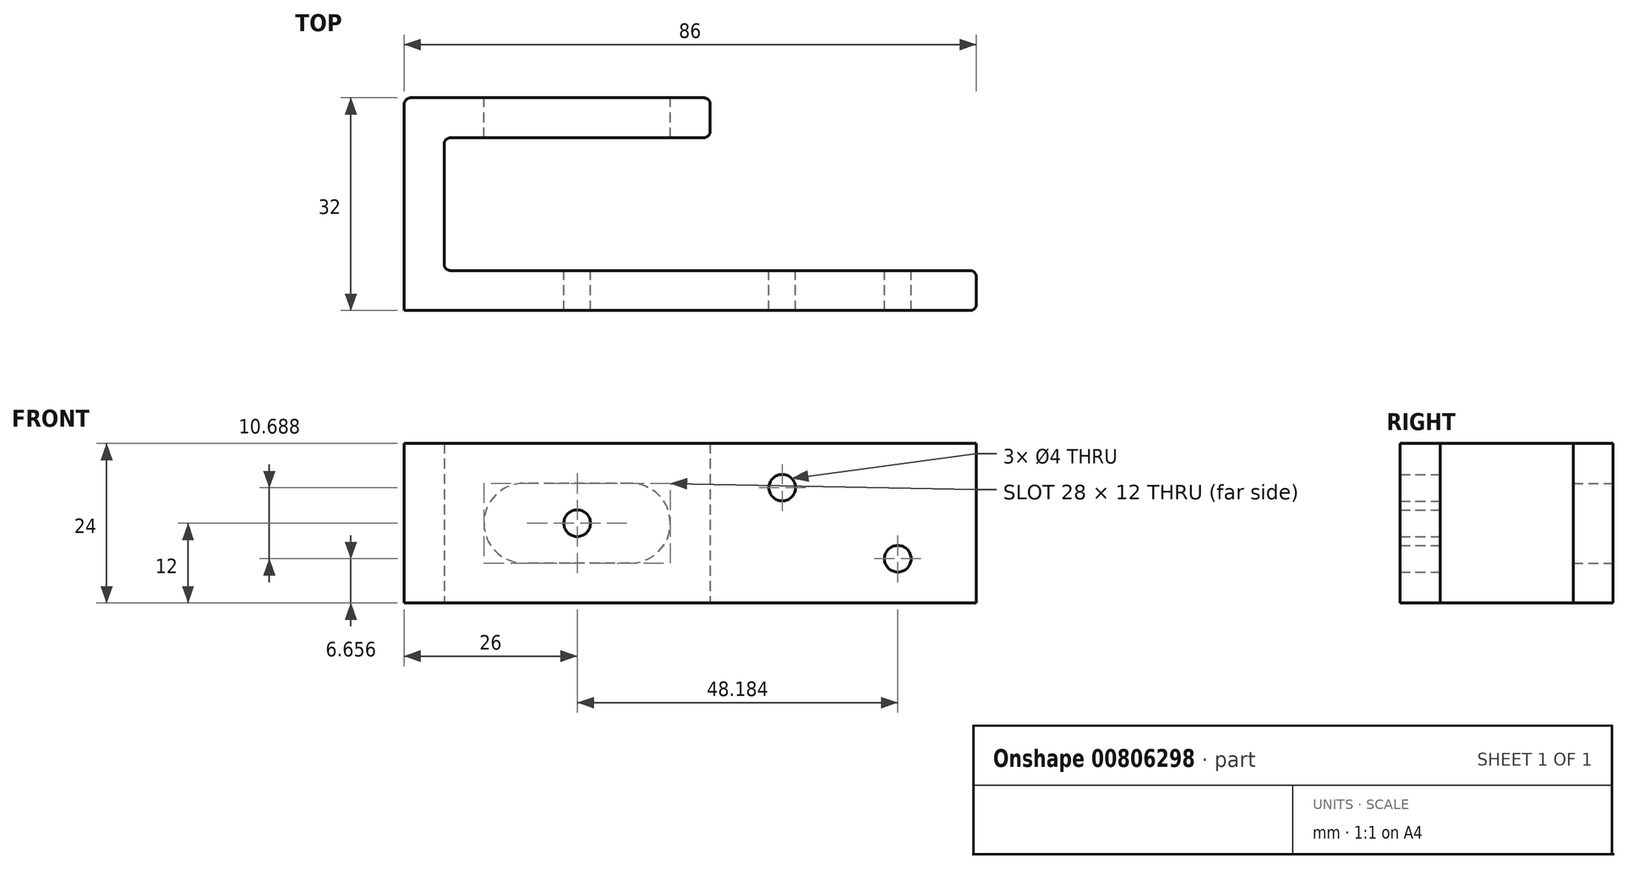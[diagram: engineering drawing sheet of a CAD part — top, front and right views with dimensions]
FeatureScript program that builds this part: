
annotation { "Feature Type Name" : "Feature", "Feature Type Description" : "" }
export const myFeature = defineFeature(function(context is Context, id is Id, definition is map)
    precondition{}
    {
        {
            var Q0;
            Q0=qCreatedBy(makeId("Top.planeOp"),FACE);
            var sketch = newSketch(context, id + "F0", { "sketchPlane" : qUnion([Q0])});
            skLineSegment(sketch, "E0.bottom", {"start": v(0, 0) * mm, "end": v(-6, 0) * mm});
            skLineSegment(sketch, "E0.top", {"start": v(0, 32) * mm, "end": v(-6, 32) * mm});
            skLineSegment(sketch, "E0.left", {"start": v(0, 0) * mm, "end": v(0, 32) * mm});
            skLineSegment(sketch, "E0.right", {"start": v(-6, 0) * mm, "end": v(-6, 32) * mm});
            skLineSegment(sketch, "E1.bottom", {"start": v(0, 32) * mm, "end": v(40, 32) * mm});
            skLineSegment(sketch, "E1.top", {"start": v(0, 26) * mm, "end": v(40, 26) * mm});
            skLineSegment(sketch, "E1.left", {"start": v(0, 32) * mm, "end": v(0, 26) * mm});
            skLineSegment(sketch, "E1.right", {"start": v(40, 32) * mm, "end": v(40, 26) * mm});
            skLineSegment(sketch, "E2.bottom", {"start": v(0, 0) * mm, "end": v(80, 0) * mm});
            skLineSegment(sketch, "E2.top", {"start": v(0, 6) * mm, "end": v(80, 6) * mm});
            skLineSegment(sketch, "E2.left", {"start": v(0, 0) * mm, "end": v(0, 6) * mm});
            skLineSegment(sketch, "E2.right", {"start": v(80, 0) * mm, "end": v(80, 6) * mm});
            skSolve(sketch);
        }
        {
            var Q0;
            Q0=makeQuery(id+"F0.imprint","IMPRINT",FACE,{"disambiguationData":[TD([[makeQuery(id+"F0.imprint","IMPRINT",EDGE,{"derivedFrom":sQuery(id+"F0.wireOp",EDGE,"E1.bottom")}),-1.0]])]});
            var Q1;
            Q1=makeQuery(id+"F0.imprint","IMPRINT",FACE,{"disambiguationData":[TD([[makeQuery(id+"F0.imprint","IMPRINT",EDGE,{"derivedFrom":sQuery(id+"F0.wireOp",EDGE,"E2.bottom")}),1.0]])]});
            var Q2;
            Q2=makeQuery(id+"F0.imprint","IMPRINT",FACE,{"disambiguationData":[TD([[makeQuery(id+"F0.imprint","IMPRINT",EDGE,{"derivedFrom":sQuery(id+"F0.wireOp",EDGE,"E0.bottom")}),-1.0]])]});
            extrude(context, id + "F1", {"entities" : qUnion([Q0, Q1, Q2]), "depth" : 24 * mm, "offsetDistance" : 25.4 * mm});
        }
        {
            var Q0;
            Q0=makeQuery(id+"F1.opExtrude","SWEPT_EDGE",EDGE,{"disambiguationData":[OSD([sQuery(id+"F0.wireOp",EDGE,"E0.left"),sQuery(id+"F0.wireOp",EDGE,"E2.top"),sQuery(id+"F0.wireOp",EDGE,"E2.left")])]});
            fillet(context, id + "F2", {"entities" : qUnion([Q0]), "radius" : 1 * mm, "tangentPropagation" : true, "allowEdgeOverflow" : false});
        }
        {
            var Q0;
            Q0=makeQuery(id+"F1.opExtrude","SWEPT_EDGE",EDGE,{"disambiguationData":[OSD([sQuery(id+"F0.wireOp",EDGE,"E2.top"),sQuery(id+"F0.wireOp",EDGE,"E2.right")])]});
            fillet(context, id + "F3", {"entities" : qUnion([Q0]), "radius" : 1 * mm, "tangentPropagation" : true, "allowEdgeOverflow" : false});
        }
        {
            var Q0;
            Q0=makeQuery(id+"F1.opExtrude","SWEPT_EDGE",EDGE,{"disambiguationData":[OSD([sQuery(id+"F0.wireOp",EDGE,"E2.bottom"),sQuery(id+"F0.wireOp",EDGE,"E2.right")])]});
            fillet(context, id + "F4", {"entities" : qUnion([Q0]), "radius" : 1 * mm, "tangentPropagation" : true, "allowEdgeOverflow" : false});
        }
        {
            var Q0;
            Q0=makeQuery(id+"F1.opExtrude","SWEPT_EDGE",EDGE,{"disambiguationData":[OSD([sQuery(id+"F0.wireOp",EDGE,"E0.left"),sQuery(id+"F0.wireOp",EDGE,"E1.top"),sQuery(id+"F0.wireOp",EDGE,"E1.left")])]});
            fillet(context, id + "F5", {"entities" : qUnion([Q0]), "radius" : 1 * mm, "tangentPropagation" : true, "allowEdgeOverflow" : false});
        }
        {
            var Q0;
            Q0=makeQuery(id+"F1.opExtrude","SWEPT_EDGE",EDGE,{"disambiguationData":[OSD([sQuery(id+"F0.wireOp",EDGE,"E1.bottom"),sQuery(id+"F0.wireOp",EDGE,"E1.right")])]});
            fillet(context, id + "F6", {"entities" : qUnion([Q0]), "radius" : 1 * mm, "tangentPropagation" : true, "allowEdgeOverflow" : false});
        }
        {
            var Q0;
            Q0=makeQuery(id+"F1.opExtrude","SWEPT_EDGE",EDGE,{"disambiguationData":[OSD([sQuery(id+"F0.wireOp",EDGE,"E1.top"),sQuery(id+"F0.wireOp",EDGE,"E1.right")])]});
            fillet(context, id + "F7", {"entities" : qUnion([Q0]), "radius" : 1 * mm, "tangentPropagation" : true, "allowEdgeOverflow" : false});
        }
        {
            var Q0;
            Q0=makeQuery(id+"F1.opExtrude","SWEPT_EDGE",EDGE,{"disambiguationData":[OSD([sQuery(id+"F0.wireOp",EDGE,"E0.top"),sQuery(id+"F0.wireOp",EDGE,"E0.right")])]});
            fillet(context, id + "F8", {"entities" : qUnion([Q0]), "radius" : 1 * mm, "tangentPropagation" : true, "allowEdgeOverflow" : false});
        }
        {
            var Q0;
            Q0=makeQuery(id+"F1.opExtrude","SWEPT_FACE",FACE,{"disambiguationData":[OSD([sQuery(id+"F0.wireOp",EDGE,"E0.top"),sQuery(id+"F0.wireOp",EDGE,"E1.bottom")])]});
            var sketch = newSketch(context, id + "F9", { "sketchPlane" : qUnion([Q0])});
            skLineSegment(sketch, "E3.bottom", {"start": v(-39, 24) * mm, "end": v(5, 24) * mm, "construction": true});
            skLineSegment(sketch, "E3.top", {"start": v(-39, 0) * mm, "end": v(5, 0) * mm, "construction": true});
            skLineSegment(sketch, "E3.left", {"start": v(-39, 24) * mm, "end": v(-39, 0) * mm, "construction": true});
            skLineSegment(sketch, "E3.right", {"start": v(5, 24) * mm, "end": v(5, 0) * mm, "construction": true});
            skLineSegment(sketch, "E4", {"start": v(5, 12) * mm, "end": v(-39, 12) * mm, "construction": true});
            skCircle(sketch, "E5", {"center": v(-28, 12) * mm, "radius": 6 * mm});
            skCircle(sketch, "E6", {"center": v(-12, 12) * mm, "radius": 6 * mm});
            skLineSegment(sketch, "E7.bottom", {"start": v(-28, 18) * mm, "end": v(-12, 18) * mm});
            skLineSegment(sketch, "E7.top", {"start": v(-28, 6) * mm, "end": v(-12, 6) * mm});
            skLineSegment(sketch, "E7.left", {"start": v(-28, 18) * mm, "end": v(-28, 6) * mm});
            skLineSegment(sketch, "E7.right", {"start": v(-12, 18) * mm, "end": v(-12, 6) * mm});
            skSolve(sketch);
        }
        {
            var Q0;
            Q0 = qSketchRegion(id + "F9", true);
            extrude(context, id + "F10", {"entities" : qUnion([Q0]), "operationType" : NewBodyOperationType.REMOVE, "oppositeDirection" : true, "depth" : 6 * mm, "offsetDistance" : 25.4 * mm});
        }
        {
            var Q0;
            Q0=makeQuery(id+"F1.opExtrude","SWEPT_FACE",FACE,{"disambiguationData":[OSD([sQuery(id+"F0.wireOp",EDGE,"E2.top")])]});
            var sketch = newSketch(context, id + "F11", { "sketchPlane" : qUnion([Q0])});
            skLineSegment(sketch, "E8.bottom", {"start": v(-1, 24) * mm, "end": v(-79, 24) * mm, "construction": true});
            skLineSegment(sketch, "E8.top", {"start": v(-1, 0) * mm, "end": v(-79, 0) * mm, "construction": true});
            skLineSegment(sketch, "E8.left", {"start": v(-1, 24) * mm, "end": v(-1, 0) * mm, "construction": true});
            skLineSegment(sketch, "E8.right", {"start": v(-79, 24) * mm, "end": v(-79, 0) * mm, "construction": true});
            skLineSegment(sketch, "E9", {"start": v(-1, 12) * mm, "end": v(-20, 12) * mm, "construction": true});
            skCircle(sketch, "E10", {"center": v(-20, 12) * mm, "radius": 2 * mm});
            skLineSegment(sketch, "E11", {"start": v(-40, 24) * mm, "end": v(-79, 0) * mm, "construction": true});
            skLineSegment(sketch, "E12", {"start": v(-79, 0) * mm, "end": v(-68.18, 6.66) * mm, "construction": true});
            skLineSegment(sketch, "E13", {"start": v(-40, 24) * mm, "end": v(-50.82, 17.34) * mm, "construction": true});
            skCircle(sketch, "E14", {"center": v(-68.18, 6.66) * mm, "radius": 2 * mm});
            skCircle(sketch, "E15", {"center": v(-50.82, 17.34) * mm, "radius": 2 * mm});
            skSolve(sketch);
        }
        {
            var Q0;
            Q0 = qSketchRegion(id + "F11", true);
            extrude(context, id + "F12", {"entities" : qUnion([Q0]), "operationType" : NewBodyOperationType.REMOVE, "oppositeDirection" : true, "depth" : 6 * mm, "offsetDistance" : 25.4 * mm});
        }
    });
